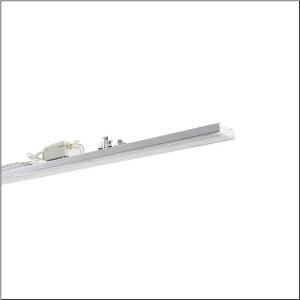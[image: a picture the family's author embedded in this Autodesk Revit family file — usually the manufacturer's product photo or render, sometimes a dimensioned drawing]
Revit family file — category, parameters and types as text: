
# Revit family: licross_r__21_recessed_mo_52te11dv4dxg_417d
name_source: partatom
category: Lighting Fixtures
units: mm (PartAtom-declared; Revit-internal decimal feet)

## family parameters
Cut with Voids When Loaded = No
Host = Face
Light Source = No
Part Type = Normal
Room Calculation Point = No
Round Connector Dimension = Use Diameter
Shared = No

## types (1)
- --- (1 x LED, 13000 lm, 72.2 W, 4000K)
    Apparent Load = 72 VA
    CIE Flux Codes = 89 96 99 100 100
    Color Rendering = 80
    Color Temperature = 4000K
    Default Elevation = 1800 mm
    Description = Licross® 21 Recessed MO, luminaire insert, of sheet steel, galvanised, coil coated, white, length: 2.250mm, width: 66mm, height: 67mm, LED rated luminous flux: 13.000lm, light colour: 840, control gear: DALI 2, with plug, 5-pole, with phase selection, mains connection: 220..240V, AC, 50/60Hz, rated input power: 72W, halogen-free wiring, primary light control with lens, of plastic, primary optical cover: cover, of PMMA, light emission: direct distribution, primary light characteristic: symmetric, protection rating (complete): IP54, insulation class (complete): insulation class I (protective earthing), certification: CE, ENEC, VDE, UKCA, protection symbol: D if used in an environment with non-conductive dust loads with corresponding accessories, impact resistance: IK06, permissible ambient temperature for indoor applications: -25..+35°C, corresponds to IFS (International Featured Standards) requirements for safety and quality in the food industry, reducing of maximum allowable ambient temperature of 5°C with ceiling mounting, LABS conformity tested according to VDMA 24364:2018-05, packaging unit: 1 piece
    Height = 58 mm
    Lamp = 1 x LED
    Lamp Light Flux = 13000 lm
    Lamp Power = 72.2 W
    Lamp count = 1
    Length = 2250 mm
    Luminous efficacy = 180 lm/W
    Manufacturer = Siteco
    ModVariant = No
    Model = 52TE11DV4DXG
    Mounting Place = Ceiling
    Mounting Type = Pendant
    Number of Poles = 1
    OnlyDefault = Yes
    Power Factor = 1
    Product Name = Licross® 21 Recessed MO
    Product group = luminaire insert
    ProductGroupID = 901
    Protection Class = Protection class I
    Protection Degree = IP 54
    RLX_Detail_Level = 1
    RLX_Emergency_Light_Flux = 0 lm
    RLX_Emergency_Type = 0
    RLX_Emergency_Type_DB = No
    RlxData = <blob elided: 29525 chars, md5=a20049c3>
    Socket = socket
    Standby Power = 0 W
    System Light Flux = 13000 lm
    System Power = 72 W
    Type Comments = factory setting: luminous flux: 100 % | dim-lin: 254 | 329 mA
    Type Image = l_1296930.jpg
    URL = http://relux.com
    VarID = @adj_058619
    Voltage = 0 V
    Weight = 0.00 kg
    Width = 66 mm

## geometry (parser evidence)
native form markers: Blend x4, Sweep x10
no freeform markers — native parametric forms only
